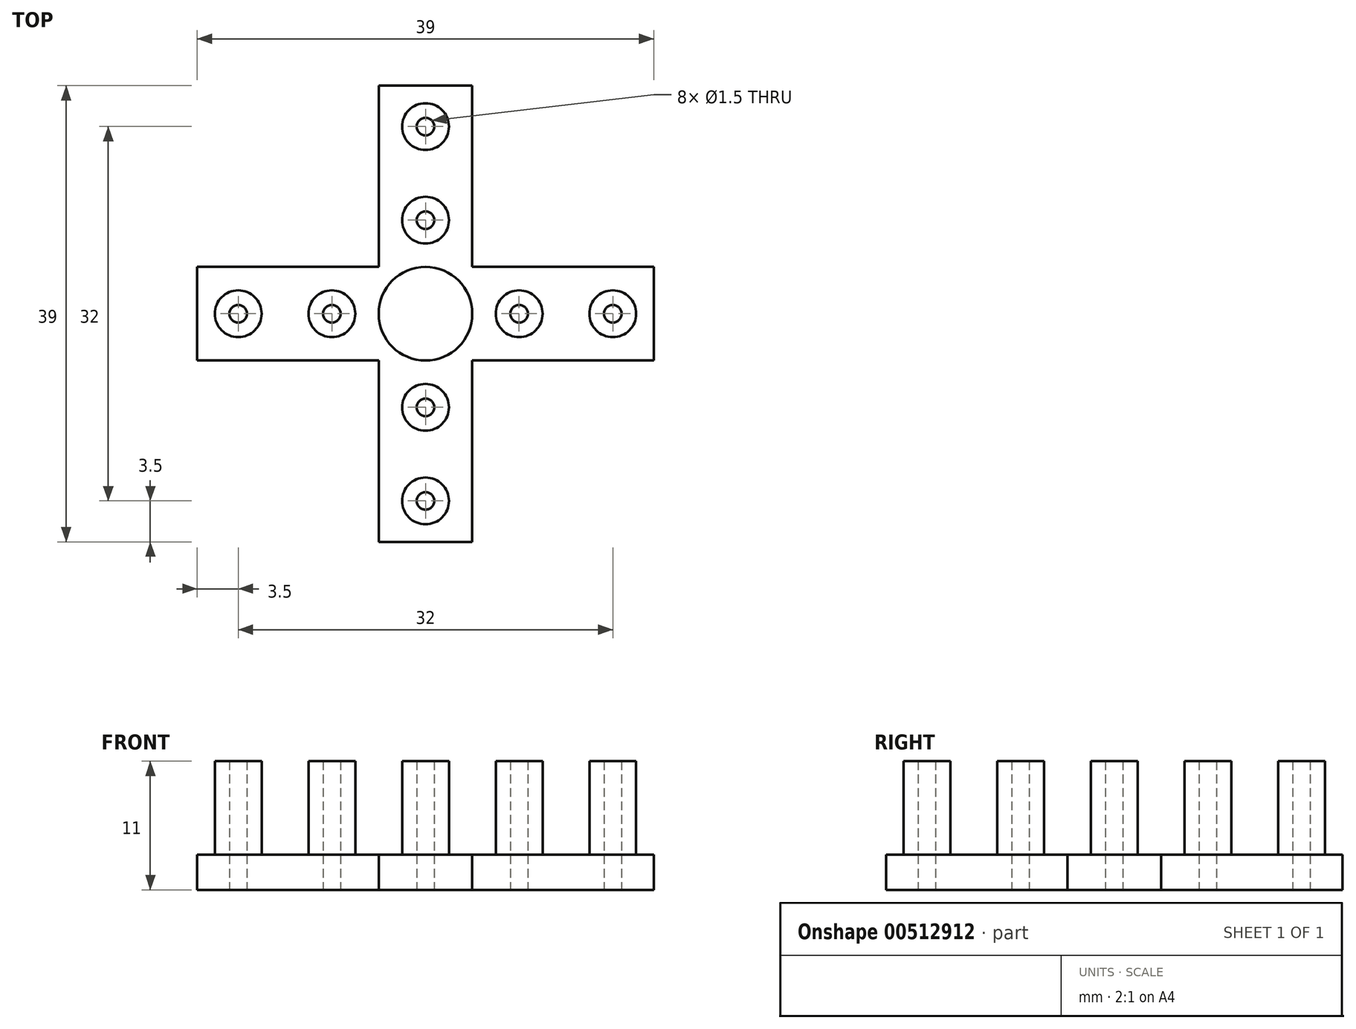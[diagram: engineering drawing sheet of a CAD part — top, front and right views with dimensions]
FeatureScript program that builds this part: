
annotation { "Feature Type Name" : "Feature", "Feature Type Description" : "" }
export const myFeature = defineFeature(function(context is Context, id is Id, definition is map)
    precondition{}
    {
        {
            var Q0;
            Q0=qCreatedBy(makeId("Top.planeOp"),FACE);
            var sketch = newSketch(context, id + "F0", { "sketchPlane" : qUnion([Q0])});
            skLineSegment(sketch, "E0.bottom", {"start": v(-4, 19.5) * mm, "end": v(4, 19.5) * mm});
            skLineSegment(sketch, "E0.top", {"start": v(-4, -19.5) * mm, "end": v(4, -19.5) * mm});
            skLineSegment(sketch, "E0.left", {"start": v(-4, 19.5) * mm, "end": v(-4, -19.5) * mm});
            skLineSegment(sketch, "E0.right", {"start": v(4, 19.5) * mm, "end": v(4, -19.5) * mm});
            skLineSegment(sketch, "E1.bottom", {"start": v(-19.5, 4) * mm, "end": v(19.5, 4) * mm});
            skLineSegment(sketch, "E1.top", {"start": v(-19.5, -4) * mm, "end": v(19.5, -4) * mm});
            skLineSegment(sketch, "E1.left", {"start": v(-19.5, 4) * mm, "end": v(-19.5, -4) * mm});
            skLineSegment(sketch, "E1.right", {"start": v(19.5, 4) * mm, "end": v(19.5, -4) * mm});
            skSolve(sketch);
        }
        {
            var Q0;
            {var subQ0=sQuery(id+"F0.wireOp",EDGE,"E1.bottom");var subQ1=sQuery(id+"F0.wireOp",EDGE,"E0.left");var subQ2=makeQuery(id+"F0.imprint","INTERSECT",VERTEX,{"derivedFrom":[subQ1,subQ0]});Q0=makeQuery(id+"F0.imprint","IMPRINT",FACE,{"disambiguationData":[TD([[makeQuery(id+"F0.imprint","IMPRINT",EDGE,{"disambiguationData":[TD([[subQ2,-1.0]])],"derivedFrom":subQ1}),1.0]])]});}
            var Q1;
            {var subQ0=sQuery(id+"F0.wireOp",EDGE,"E0.bottom");Q1=makeQuery(id+"F0.imprint","IMPRINT",FACE,{"disambiguationData":[TD([[makeQuery(id+"F0.imprint","IMPRINT",EDGE,{"derivedFrom":subQ0}),-1.0]])]});}
            var Q2;
            {var subQ5=sQuery(id+"F0.wireOp",EDGE,"E1.left");Q2=makeQuery(id+"F0.imprint","IMPRINT",FACE,{"disambiguationData":[TD([[makeQuery(id+"F0.imprint","IMPRINT",EDGE,{"derivedFrom":subQ5}),1.0]])]});}
            var Q3;
            {var subQ5=sQuery(id+"F0.wireOp",EDGE,"E1.right");Q3=makeQuery(id+"F0.imprint","IMPRINT",FACE,{"disambiguationData":[TD([[makeQuery(id+"F0.imprint","IMPRINT",EDGE,{"derivedFrom":subQ5}),-1.0]])]});}
            var Q4;
            {var subQ0=sQuery(id+"F0.wireOp",EDGE,"E0.top");Q4=makeQuery(id+"F0.imprint","IMPRINT",FACE,{"disambiguationData":[TD([[makeQuery(id+"F0.imprint","IMPRINT",EDGE,{"derivedFrom":subQ0}),1.0]])]});}
            extrude(context, id + "F1", {"entities" : qUnion([Q0, Q1, Q2, Q3, Q4]), "depth" : 3 * mm});
        }
        {
            var Q0;
            Q0=qCreatedBy(makeId("Top.planeOp"),FACE);
            var sketch = newSketch(context, id + "F2", { "sketchPlane" : qUnion([Q0])});
            skPoint(sketch, "E2", {"position": v(0, 0) * mm});
            skSolve(sketch);
        }
        {
            var Q0;
            Q0=sQuery(id+"F2.wireOp",VERTEX,"E2");
            var Q1;
            Q1=makeQuery(id+"F1.opExtrude","SWEPT_BODY",BODY,{"disambiguationData":[OSD([sQuery(id+"F0.wireOp",EDGE,"E0.bottom"),sQuery(id+"F0.wireOp",EDGE,"E0.top"),sQuery(id+"F0.wireOp",EDGE,"E0.left"),sQuery(id+"F0.wireOp",EDGE,"E0.right"),sQuery(id+"F0.wireOp",EDGE,"E1.bottom"),sQuery(id+"F0.wireOp",EDGE,"E1.top"),sQuery(id+"F0.wireOp",EDGE,"E1.left"),sQuery(id+"F0.wireOp",EDGE,"E1.right")])]});
            hole(context, id + "F3", {"style" : HoleStyle.SIMPLE, "endStyle" : HoleEndStyle.THROUGH, "oppositeDirection" : true, "holeDiameter" : 8 * mm, "majorDiameter" : 5 * mm, "isTappedThrough" : true, "tappedDepth" : 12 * mm, "tapClearance" : 3, "startFromSketch" : true, "locations" : qUnion([Q0]), "scope" : qUnion([Q1])});
        }
        {
            var Q0;
            Q0=makeQuery(id+"F1.opExtrude","CAP_FACE",FACE,{"disambiguationData":[OSD([sQuery(id+"F0.wireOp",EDGE,"E0.bottom"),sQuery(id+"F0.wireOp",EDGE,"E0.top"),sQuery(id+"F0.wireOp",EDGE,"E0.left"),sQuery(id+"F0.wireOp",EDGE,"E0.right"),sQuery(id+"F0.wireOp",EDGE,"E1.bottom"),sQuery(id+"F0.wireOp",EDGE,"E1.top"),sQuery(id+"F0.wireOp",EDGE,"E1.left"),sQuery(id+"F0.wireOp",EDGE,"E1.right")])],"isStart":false});
            var sketch = newSketch(context, id + "F4", { "sketchPlane" : qUnion([Q0])});
            skPoint(sketch, "E3", {"position": v(-8, 0) * mm});
            skPoint(sketch, "E4", {"position": v(-16, 0) * mm});
            skCircle(sketch, "E5", {"center": v(-16, 0) * mm, "radius": 2 * mm});
            skCircle(sketch, "E6", {"center": v(-8, 0) * mm, "radius": 2 * mm});
            skCircle(sketch, "E7.1.0", {"center": v(0, -8) * mm, "radius": 2 * mm});
            skCircle(sketch, "E7.1.1", {"center": v(0, -16) * mm, "radius": 2 * mm});
            skCircle(sketch, "E7.2.0", {"center": v(8, 0) * mm, "radius": 2 * mm});
            skCircle(sketch, "E7.2.1", {"center": v(16, 0) * mm, "radius": 2 * mm});
            skCircle(sketch, "E7.3.0", {"center": v(0, 8) * mm, "radius": 2 * mm});
            skCircle(sketch, "E7.3.1", {"center": v(0, 16) * mm, "radius": 2 * mm});
            skPoint(sketch, "E7.center", {"position": v(0, 0) * mm});
            skSolve(sketch);
        }
        {
            var Q0;
            Q0 = qSketchRegion(id + "F4", true);
            extrude(context, id + "F5", {"entities" : qUnion([Q0]), "operationType" : NewBodyOperationType.ADD, "depth" : 8 * mm, "offsetDistance" : 25 * mm});
        }
        {
            var Q0;
            Q0=qCreatedBy(makeId("Top.planeOp"),FACE);
            var sketch = newSketch(context, id + "F6", { "sketchPlane" : qUnion([Q0])});
            skPoint(sketch, "E8", {"position": v(0, 16) * mm});
            skPoint(sketch, "E9", {"position": v(0, 8) * mm});
            skPoint(sketch, "E10", {"position": v(-8, 0) * mm});
            skPoint(sketch, "E11", {"position": v(-16, 0) * mm});
            skPoint(sketch, "E12", {"position": v(8, 0) * mm});
            skPoint(sketch, "E13", {"position": v(16, 0) * mm});
            skPoint(sketch, "E14", {"position": v(0, -8) * mm});
            skPoint(sketch, "E15", {"position": v(0, -16) * mm});
            skSolve(sketch);
        }
        {
            var Q0;
            Q0=sQuery(id+"F6.wireOp",VERTEX,"E11");
            var Q1;
            Q1=sQuery(id+"F6.wireOp",VERTEX,"E10");
            var Q2;
            Q2=sQuery(id+"F6.wireOp",VERTEX,"E8");
            var Q3;
            Q3=sQuery(id+"F6.wireOp",VERTEX,"E9");
            var Q4;
            Q4=sQuery(id+"F6.wireOp",VERTEX,"E12");
            var Q5;
            Q5=sQuery(id+"F6.wireOp",VERTEX,"E13");
            var Q6;
            Q6=sQuery(id+"F6.wireOp",VERTEX,"E14");
            var Q7;
            Q7=sQuery(id+"F6.wireOp",VERTEX,"E15");
            var Q8;
            Q8=makeQuery(id+"F1.opExtrude","SWEPT_BODY",BODY,{"disambiguationData":[OSD([sQuery(id+"F0.wireOp",EDGE,"E0.bottom"),sQuery(id+"F0.wireOp",EDGE,"E0.top"),sQuery(id+"F0.wireOp",EDGE,"E0.left"),sQuery(id+"F0.wireOp",EDGE,"E0.right"),sQuery(id+"F0.wireOp",EDGE,"E1.bottom"),sQuery(id+"F0.wireOp",EDGE,"E1.top"),sQuery(id+"F0.wireOp",EDGE,"E1.left"),sQuery(id+"F0.wireOp",EDGE,"E1.right")])]});
            hole(context, id + "F7", {"style" : HoleStyle.SIMPLE, "endStyle" : HoleEndStyle.THROUGH, "oppositeDirection" : true, "holeDiameter" : 1.5 * mm, "majorDiameter" : 5 * mm, "isTappedThrough" : true, "tappedDepth" : 12 * mm, "tapClearance" : 3, "startFromSketch" : true, "locations" : qUnion([Q0, Q1, Q2, Q3, Q4, Q5, Q6, Q7]), "scope" : qUnion([Q8])});
        }
    });
